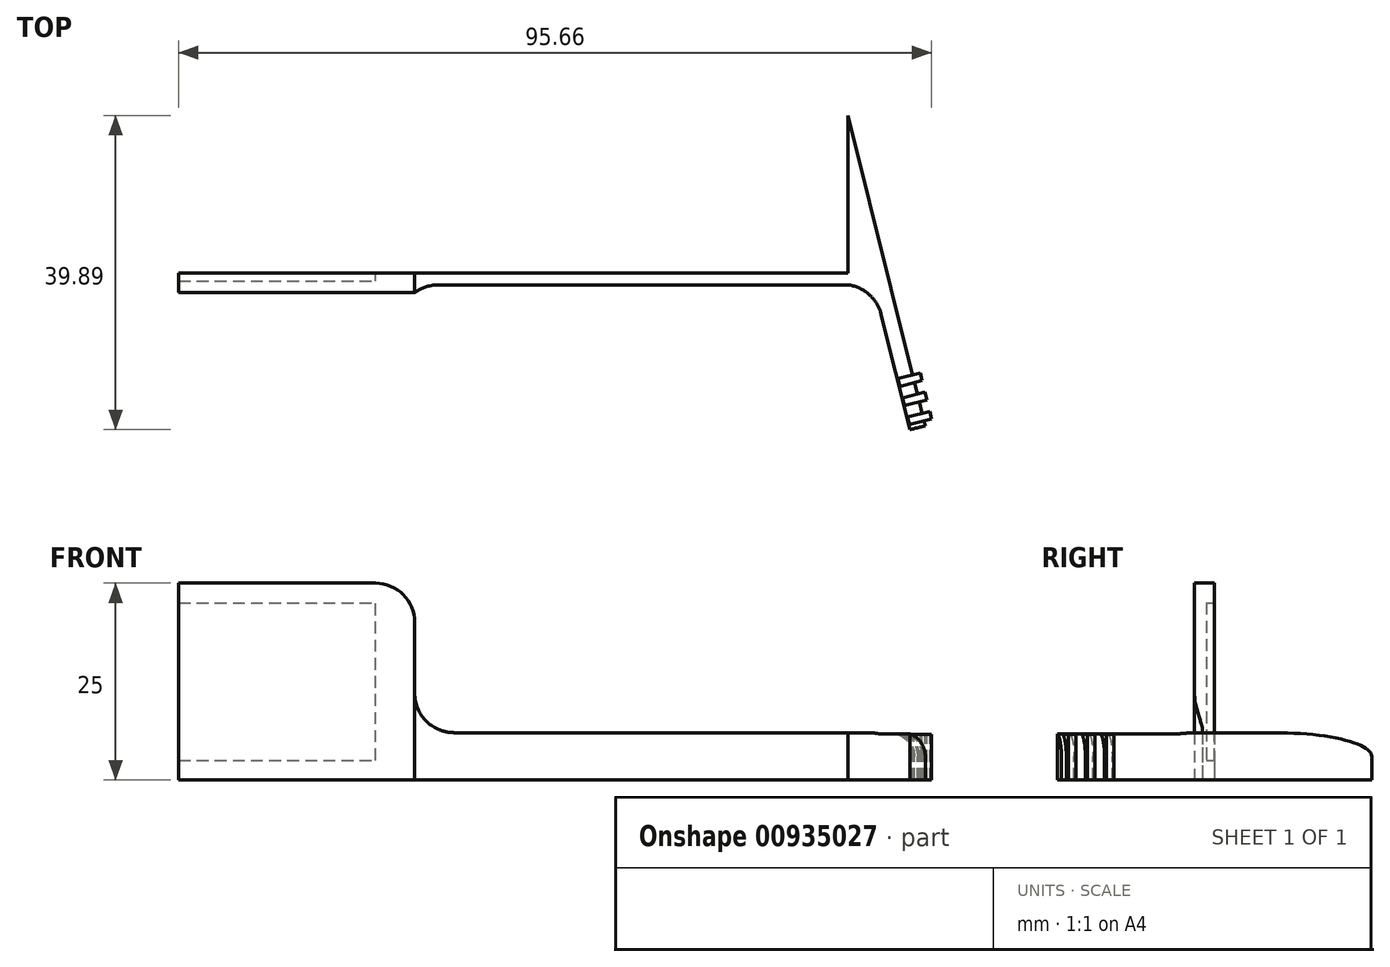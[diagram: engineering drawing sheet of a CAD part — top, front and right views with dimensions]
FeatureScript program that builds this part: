
annotation { "Feature Type Name" : "Feature", "Feature Type Description" : "" }
export const myFeature = defineFeature(function(context is Context, id is Id, definition is map)
    precondition{}
    {
        {
            var Q0;
            Q0=qCreatedBy(makeId("Top.planeOp"),FACE);
            var sketch = newSketch(context, id + "F0", { "sketchPlane" : qUnion([Q0])});
            skLineSegment(sketch, "E0.bottom", {"start": v(0, 0) * mm, "end": v(-85, 0) * mm});
            skLineSegment(sketch, "E0.top", {"start": v(0, -1.5) * mm, "end": v(-85, -1.5) * mm});
            skLineSegment(sketch, "E0.left", {"start": v(0, 0) * mm, "end": v(0, -1.5) * mm});
            skLineSegment(sketch, "E0.right", {"start": v(-85, 0) * mm, "end": v(-85, -1.5) * mm});
            skLineSegment(sketch, "E1", {"start": v(0, 0) * mm, "end": v(0, 20) * mm});
            skLineSegment(sketch, "E2", {"start": v(0, 0) * mm, "end": v(5, 0) * mm, "construction": true});
            skLineSegment(sketch, "E3", {"start": v(0, 20) * mm, "end": v(5, 0) * mm});
            skLineSegment(sketch, "E4", {"start": v(5, 0) * mm, "end": v(9.85, -19.4) * mm});
            skLineSegment(sketch, "E5", {"start": v(9.85, -19.4) * mm, "end": v(7.91, -19.89) * mm});
            skLineSegment(sketch, "E6", {"start": v(7.91, -19.89) * mm, "end": v(3.22, -1.11) * mm});
            skLineSegment(sketch, "E7", {"start": v(0, -1.5) * mm, "end": v(3.22, -1.11) * mm});
            skSolve(sketch);
        }
        {
            var Q0;
            Q0=makeQuery(id+"F0.imprint","IMPRINT",FACE,{"disambiguationData":[TD([[makeQuery(id+"F0.imprint","IMPRINT",EDGE,{"derivedFrom":sQuery(id+"F0.wireOp",EDGE,"E0.bottom")}),1.0]])]});
            var Q1;
            Q1=makeQuery(id+"F0.imprint","IMPRINT",FACE,{"disambiguationData":[TD([[makeQuery(id+"F0.imprint","IMPRINT",EDGE,{"derivedFrom":sQuery(id+"F0.wireOp",EDGE,"E0.left")}),1.0]])]});
            extrude(context, id + "F1", {"entities" : qUnion([Q0, Q1]), "depth" : 6 * mm, "offsetDistance" : 25 * mm});
        }
        {
            var Q0;
            Q0=makeQuery(id+"F8Hdey2kUb04CLZ_1.boolean.opBoolean","MERGE",FACE,{"derivedFrom":[makeQuery(id+"F1.opExtrude","SWEPT_FACE",FACE,{"disambiguationData":[OSD([sQuery(id+"F0.wireOp",EDGE,"E0.bottom")])]}),makeQuery(id+"F8Hdey2kUb04CLZ_1.opExtrude","CAP_FACE",FACE,{"disambiguationData":[OSD([sQuery(id+"F0.wireOp",EDGE,"E0.top"),sQuery(id+"FDe1htsatOI701G_1.wireOp",EDGE,"8rJ1pwWU-0Bg1-5z3G-cBGB-ATapcbajXxPj"),sQuery(id+"FDe1htsatOI701G_1.wireOp",EDGE,"0k21qJGq-c9eN-bHA8-YZJg-b3gz2aeNbx6B"),sQuery(id+"FDe1htsatOI701G_1.wireOp",EDGE,"J7W5i0Tx-JJDw-OMGW-2mcu-rQrk15kmPtQ6")])],"isStart":false})]});
            var sketch = newSketch(context, id + "F2", { "sketchPlane" : qUnion([Q0])});
            skLineSegment(sketch, "E8.0", {"start": v(0, 0) * mm, "end": v(85, 0) * mm});
            skLineSegment(sketch, "E9.bottom", {"start": v(85, 2.5) * mm, "end": v(60, 2.5) * mm});
            skLineSegment(sketch, "E9.top", {"start": v(85, 22.5) * mm, "end": v(60, 22.5) * mm});
            skLineSegment(sketch, "E9.left", {"start": v(85, 2.5) * mm, "end": v(85, 22.5) * mm});
            skLineSegment(sketch, "E9.right", {"start": v(60, 2.5) * mm, "end": v(60, 22.5) * mm});
            skLineSegment(sketch, "E10", {"start": v(55, 25) * mm, "end": v(85, 25) * mm});
            skLineSegment(sketch, "E11", {"start": v(85, 25) * mm, "end": v(85, 0) * mm});
            skLineSegment(sketch, "E12", {"start": v(85, 0) * mm, "end": v(55, 0) * mm});
            skLineSegment(sketch, "E13", {"start": v(55, 25) * mm, "end": v(55, 0) * mm});
            skSolve(sketch);
        }
        {
            var Q0;
            {var subQ0=sQuery(id+"F2.wireOp",EDGE,"E9.bottom");Q0=makeQuery(id+"F2.imprint","IMPRINT",FACE,{"disambiguationData":[TD([[makeQuery(id+"F2.imprint","IMPRINT",EDGE,{"derivedFrom":subQ0}),-1.0]])]});}
            var Q1;
            {var subQ1=sQuery(id+"F2.wireOp",EDGE,"E9.bottom");Q1=makeQuery(id+"F2.imprint","IMPRINT",FACE,{"disambiguationData":[TD([[makeQuery(id+"F2.imprint","IMPRINT",EDGE,{"derivedFrom":subQ1}),1.0]])]});}
            var Q2;
            {var subQ0=sQuery(id+"F2.wireOp",EDGE,"E9.top");Q2=makeQuery(id+"F2.imprint","IMPRINT",FACE,{"disambiguationData":[TD([[makeQuery(id+"F2.imprint","IMPRINT",EDGE,{"derivedFrom":subQ0}),1.0]])]});}
            var Q3;
            {var subQ1=sQuery(id+"F2.wireOp",EDGE,"E9.top");Q3=makeQuery(id+"F2.imprint","IMPRINT",FACE,{"disambiguationData":[TD([[makeQuery(id+"F2.imprint","IMPRINT",EDGE,{"derivedFrom":subQ1}),-1.0]])]});}
            extrude(context, id + "F3", {"entities" : qUnion([Q0, Q1, Q2, Q3]), "operationType" : NewBodyOperationType.ADD, "oppositeDirection" : true, "depth" : 2.5 * mm, "offsetDistance" : 25 * mm});
        }
        {
            var Q0;
            Q0=makeQuery(id+"F2.imprint","IMPRINT",FACE,{"disambiguationData":[TD([[makeQuery(id+"F2.imprint","IMPRINT",EDGE,{"derivedFrom":sQuery(id+"F2.wireOp",EDGE,"E9.bottom")}),-1.0]])]});
            var Q1;
            {var subQ0=sQuery(id+"F2.wireOp",EDGE,"E9.top");Q1=makeQuery(id+"F2.imprint","IMPRINT",FACE,{"disambiguationData":[TD([[makeQuery(id+"F2.imprint","IMPRINT",EDGE,{"derivedFrom":subQ0}),1.0]])]});}
            extrude(context, id + "F4", {"entities" : qUnion([Q0, Q1]), "operationType" : NewBodyOperationType.REMOVE, "oppositeDirection" : true, "depth" : 1 * mm, "offsetDistance" : 25 * mm});
        }
        {
            var Q0;
            Q0=makeQuery(id+"F3.opExtrude","SWEPT_EDGE",EDGE,{"disambiguationData":[OSD([sQuery(id+"F2.wireOp",EDGE,"E10"),sQuery(id+"F2.wireOp",EDGE,"E13")])]});
            var Q1;
            Q1=makeQuery(id+"F1.opExtrude","SWEPT_EDGE",EDGE,{"disambiguationData":[OSD([sQuery(id+"F0.wireOp",EDGE,"E6"),sQuery(id+"F0.wireOp",EDGE,"E7")])]});
            var Q2;
            Q2=makeQuery(id+"F3.boolean.opBoolean","INTERSECT",EDGE,{"derivedFrom":[makeQuery(id+"F1.opExtrude","CAP_FACE",FACE,{"disambiguationData":[OSD([sQuery(id+"F0.wireOp",EDGE,"E0.bottom"),sQuery(id+"F0.wireOp",EDGE,"E0.top"),sQuery(id+"F0.wireOp",EDGE,"E0.right"),sQuery(id+"F0.wireOp",EDGE,"E1"),sQuery(id+"F0.wireOp",EDGE,"E3"),sQuery(id+"F0.wireOp",EDGE,"E4"),sQuery(id+"F0.wireOp",EDGE,"E5"),sQuery(id+"F0.wireOp",EDGE,"E6"),sQuery(id+"F0.wireOp",EDGE,"E7")])],"isStart":false}),makeQuery(id+"F3.opExtrude","SWEPT_FACE",FACE,{"disambiguationData":[OSD([sQuery(id+"F2.wireOp",EDGE,"E13")])]})]});
            var Q3;
            Q3=makeQuery(id+"F3.boolean.opBoolean","INTERSECT",EDGE,{"derivedFrom":[makeQuery(id+"F1.opExtrude","SWEPT_FACE",FACE,{"disambiguationData":[OSD([sQuery(id+"F0.wireOp",EDGE,"E0.top")])]}),makeQuery(id+"F3.opExtrude","SWEPT_FACE",FACE,{"disambiguationData":[OSD([sQuery(id+"F2.wireOp",EDGE,"E13")])]})]});
            fillet(context, id + "F5", {"entities" : qUnion([Q0, Q1, Q2, Q3]), "radius" : 5 * mm, "tangentPropagation" : true, "allowEdgeOverflow" : false});
        }
        {
            var Q0;
            Q0=makeQuery(id+"F1.opExtrude","CAP_EDGE",EDGE,{"disambiguationData":[OSD([sQuery(id+"F0.wireOp",EDGE,"E3"),sQuery(id+"F0.wireOp",EDGE,"E4")])],"isStart":false});
            fillet(context, id + "F6", {"entities" : qUnion([Q0]), "radius" : 3 * mm, "tangentPropagation" : true, "allowEdgeOverflow" : false});
        }
        {
            var Q0;
            Q0=makeQuery(id+"F1.opExtrude","SWEPT_FACE",FACE,{"disambiguationData":[OSD([sQuery(id+"F0.wireOp",EDGE,"E3"),sQuery(id+"F0.wireOp",EDGE,"E4")])]});
            var sketch = newSketch(context, id + "F7", { "sketchPlane" : qUnion([Q0])});
            skLineSegment(sketch, "E14.bottom", {"start": v(-20.57, 0) * mm, "end": v(-19.57, 0) * mm});
            skLineSegment(sketch, "E14.top", {"start": v(-20.57, 5.8) * mm, "end": v(-19.57, 5.8) * mm});
            skLineSegment(sketch, "E14.left", {"start": v(-20.57, 0) * mm, "end": v(-20.57, 5.8) * mm});
            skLineSegment(sketch, "E14.right", {"start": v(-19.57, 0) * mm, "end": v(-19.57, 5.8) * mm});
            skLineSegment(sketch, "E15.bottom", {"start": v(-18.07, 0) * mm, "end": v(-17.07, 0) * mm});
            skLineSegment(sketch, "E15.top", {"start": v(-18.07, 5.8) * mm, "end": v(-17.07, 5.8) * mm});
            skLineSegment(sketch, "E15.left", {"start": v(-18.07, 0) * mm, "end": v(-18.07, 5.8) * mm});
            skLineSegment(sketch, "E15.right", {"start": v(-17.07, 0) * mm, "end": v(-17.07, 5.8) * mm});
            skLineSegment(sketch, "E16.bottom", {"start": v(-15.57, 0) * mm, "end": v(-14.57, 0) * mm});
            skLineSegment(sketch, "E16.top", {"start": v(-15.57, 5.8) * mm, "end": v(-14.57, 5.8) * mm});
            skLineSegment(sketch, "E16.left", {"start": v(-15.57, 0) * mm, "end": v(-15.57, 5.8) * mm});
            skLineSegment(sketch, "E16.right", {"start": v(-14.57, 0) * mm, "end": v(-14.57, 5.8) * mm});
            skSolve(sketch);
        }
        {
            var Q0;
            {var subQ0=sQuery(id+"F7.wireOp",EDGE,"E14.top");Q0=makeQuery(id+"F7.imprint","IMPRINT",FACE,{"disambiguationData":[TD([[makeQuery(id+"F7.imprint","IMPRINT",EDGE,{"derivedFrom":subQ0}),-1.0]])]});}
            var Q1;
            {var subQ0=sQuery(id+"F7.wireOp",EDGE,"E14.bottom");Q1=makeQuery(id+"F7.imprint","IMPRINT",FACE,{"disambiguationData":[TD([[makeQuery(id+"F7.imprint","IMPRINT",EDGE,{"derivedFrom":subQ0}),-1.0]])]});}
            var Q2;
            {var subQ0=sQuery(id+"F7.wireOp",EDGE,"E15.bottom");Q2=makeQuery(id+"F7.imprint","IMPRINT",FACE,{"disambiguationData":[TD([[makeQuery(id+"F7.imprint","IMPRINT",EDGE,{"derivedFrom":subQ0}),-1.0]])]});}
            var Q3;
            {var subQ0=sQuery(id+"F7.wireOp",EDGE,"E15.top");Q3=makeQuery(id+"F7.imprint","IMPRINT",FACE,{"disambiguationData":[TD([[makeQuery(id+"F7.imprint","IMPRINT",EDGE,{"derivedFrom":subQ0}),-1.0]])]});}
            var Q4;
            {var subQ0=sQuery(id+"F7.wireOp",EDGE,"E16.bottom");Q4=makeQuery(id+"F7.imprint","IMPRINT",FACE,{"disambiguationData":[TD([[makeQuery(id+"F7.imprint","IMPRINT",EDGE,{"derivedFrom":subQ0}),-1.0]])]});}
            var Q5;
            {var subQ0=sQuery(id+"F7.wireOp",EDGE,"E16.top");Q5=makeQuery(id+"F7.imprint","IMPRINT",FACE,{"disambiguationData":[TD([[makeQuery(id+"F7.imprint","IMPRINT",EDGE,{"derivedFrom":subQ0}),-1.0]])]});}
            extrude(context, id + "F8", {"entities" : qUnion([Q0, Q1, Q2, Q3, Q4, Q5]), "operationType" : NewBodyOperationType.ADD, "oppositeDirection" : true, "depth" : 2 * mm, "offsetDistance" : 25 * mm});
        }
        {
            var Q0;
            {var subQ0=sQuery(id+"F7.wireOp",EDGE,"E14.top");Q0=makeQuery(id+"F7.imprint","IMPRINT",FACE,{"disambiguationData":[TD([[makeQuery(id+"F7.imprint","IMPRINT",EDGE,{"derivedFrom":subQ0}),-1.0]])]});}
            var Q1;
            {var subQ0=sQuery(id+"F7.wireOp",EDGE,"E14.bottom");Q1=makeQuery(id+"F7.imprint","IMPRINT",FACE,{"disambiguationData":[TD([[makeQuery(id+"F7.imprint","IMPRINT",EDGE,{"derivedFrom":subQ0}),-1.0]])]});}
            var Q2;
            {var subQ0=sQuery(id+"F7.wireOp",EDGE,"E15.top");Q2=makeQuery(id+"F7.imprint","IMPRINT",FACE,{"disambiguationData":[TD([[makeQuery(id+"F7.imprint","IMPRINT",EDGE,{"derivedFrom":subQ0}),-1.0]])]});}
            var Q3;
            {var subQ0=sQuery(id+"F7.wireOp",EDGE,"E15.bottom");Q3=makeQuery(id+"F7.imprint","IMPRINT",FACE,{"disambiguationData":[TD([[makeQuery(id+"F7.imprint","IMPRINT",EDGE,{"derivedFrom":subQ0}),-1.0]])]});}
            var Q4;
            {var subQ0=sQuery(id+"F7.wireOp",EDGE,"E16.top");Q4=makeQuery(id+"F7.imprint","IMPRINT",FACE,{"disambiguationData":[TD([[makeQuery(id+"F7.imprint","IMPRINT",EDGE,{"derivedFrom":subQ0}),-1.0]])]});}
            var Q5;
            {var subQ0=sQuery(id+"F7.wireOp",EDGE,"E16.bottom");Q5=makeQuery(id+"F7.imprint","IMPRINT",FACE,{"disambiguationData":[TD([[makeQuery(id+"F7.imprint","IMPRINT",EDGE,{"derivedFrom":subQ0}),-1.0]])]});}
            extrude(context, id + "F9", {"entities" : qUnion([Q0, Q1, Q2, Q3, Q4, Q5]), "operationType" : NewBodyOperationType.ADD, "depth" : 1 * mm, "offsetDistance" : 25 * mm});
        }
    });
